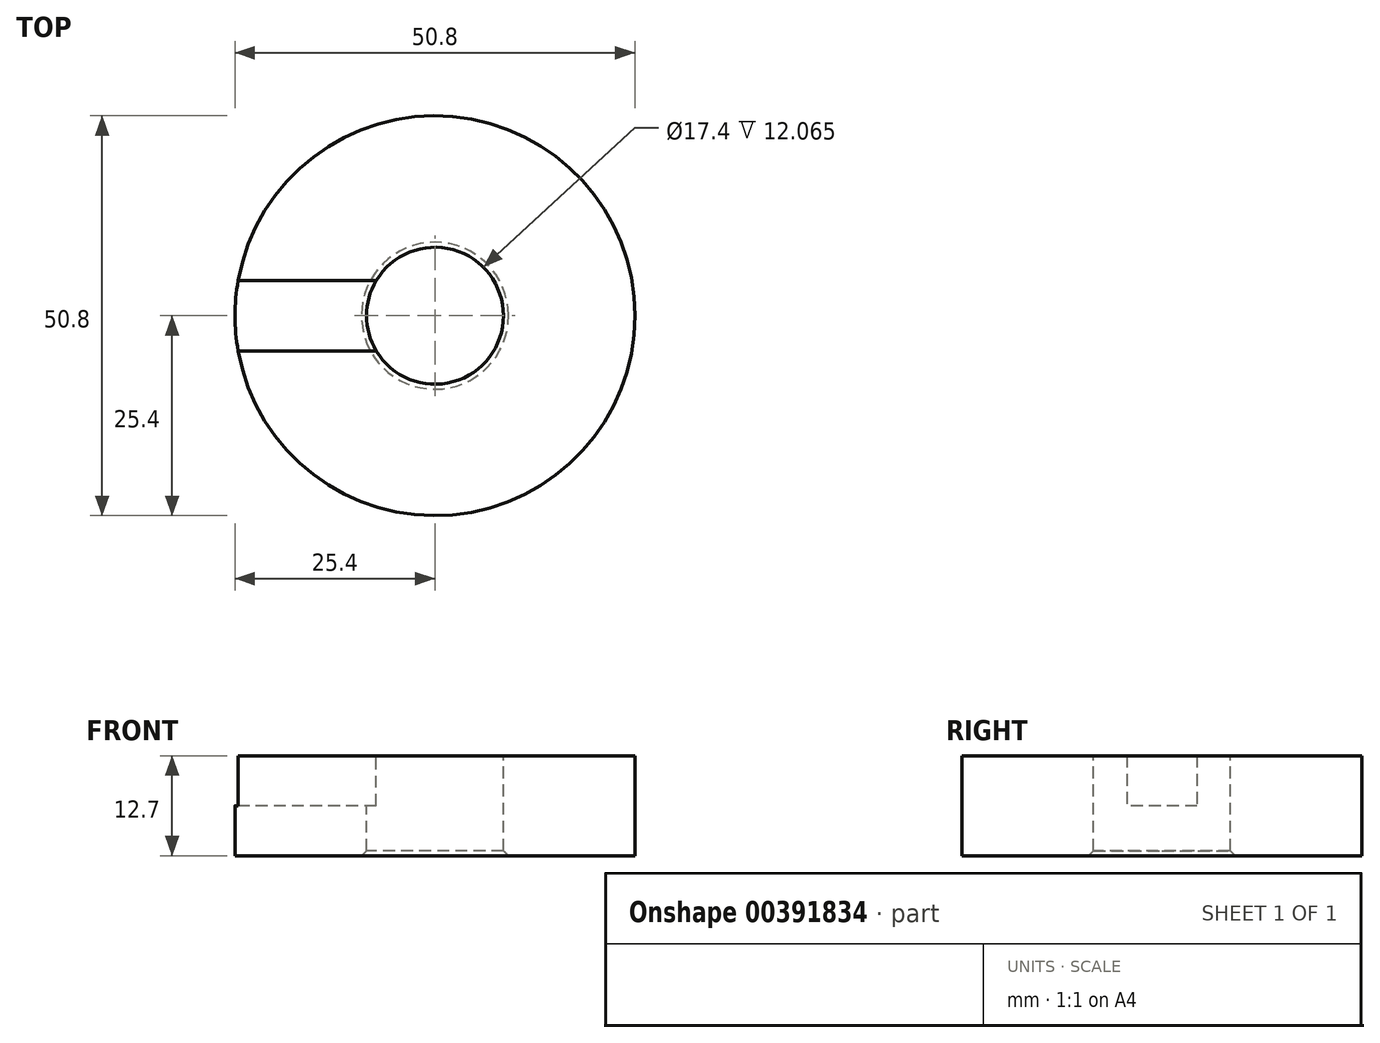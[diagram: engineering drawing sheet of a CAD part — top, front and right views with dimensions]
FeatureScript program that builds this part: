
annotation { "Feature Type Name" : "Feature", "Feature Type Description" : "" }
export const myFeature = defineFeature(function(context is Context, id is Id, definition is map)
    precondition{}
    {
        {
            var Q0;
            Q0=qCreatedBy(makeId("Top.planeOp"),FACE);
            var sketch = newSketch(context, id + "F0", { "sketchPlane" : qUnion([Q0])});
            skCircle(sketch, "E0", {"center": v(0, 0) * mm, "radius": 25.4 * mm});
            skSolve(sketch);
        }
        {
            var Q0;
            Q0 = qSketchRegion(id + "F0", true);
            extrude(context, id + "F1", {"entities" : qUnion([Q0]), "depth" : 12.7 * mm});
        }
        {
            var Q0;
            Q0=makeQuery(id+"F1.opExtrude","CAP_FACE",FACE,{"disambiguationData":[OSD([sQuery(id+"F0.wireOp",EDGE,"E0")])],"isStart":false});
            var sketch = newSketch(context, id + "F2", { "sketchPlane" : qUnion([Q0])});
            skCircle(sketch, "E1", {"center": v(0, 0) * mm, "radius": 8.7 * mm});
            skSolve(sketch);
        }
        {
            var Q0;
            Q0 = qSketchRegion(id + "F2", true);
            extrude(context, id + "F3", {"entities" : qUnion([Q0]), "operationType" : NewBodyOperationType.REMOVE, "oppositeDirection" : true, "depth" : 25.4 * mm});
        }
        {
            var Q0;
            Q0=makeQuery(id+"F1.opExtrude","CAP_FACE",FACE,{"disambiguationData":[OSD([sQuery(id+"F0.wireOp",EDGE,"E0")])],"isStart":false});
            var sketch = newSketch(context, id + "F4", { "sketchPlane" : qUnion([Q0])});
            skLineSegment(sketch, "E2.bottom", {"start": v(-7.47, -4.46) * mm, "end": v(-27.42, -4.46) * mm});
            skLineSegment(sketch, "E2.top", {"start": v(-7.47, 4.46) * mm, "end": v(-27.42, 4.46) * mm});
            skLineSegment(sketch, "E2.left", {"start": v(-7.47, -4.46) * mm, "end": v(-7.47, 4.46) * mm});
            skLineSegment(sketch, "E2.right", {"start": v(-27.42, -4.46) * mm, "end": v(-27.42, 4.46) * mm});
            skPoint(sketch, "E2.middle", {"position": v(-17.44, 0) * mm});
            skSolve(sketch);
        }
        {
            var Q0;
            Q0 = qSketchRegion(id + "F4", true);
            extrude(context, id + "F5", {"entities" : qUnion([Q0]), "operationType" : NewBodyOperationType.REMOVE, "oppositeDirection" : true, "depth" : 6.35 * mm});
        }
        {
            var Q0;
            Q0=makeQuery(id+"F3.boolean.opBoolean","INTERSECT",EDGE,{"derivedFrom":[makeQuery(id+"F1.opExtrude","CAP_FACE",FACE,{"disambiguationData":[OSD([sQuery(id+"F0.wireOp",EDGE,"E0")])],"isStart":true}),makeQuery(id+"F3.opExtrude","SWEPT_FACE",FACE,{"disambiguationData":[OSD([sQuery(id+"F2.wireOp",EDGE,"E1")])]})]});
            chamfer(context, id + "F6", {"entities" : qUnion([Q0]), "width" : 0.64 * mm, "tangentPropagation" : true});
        }
    });
